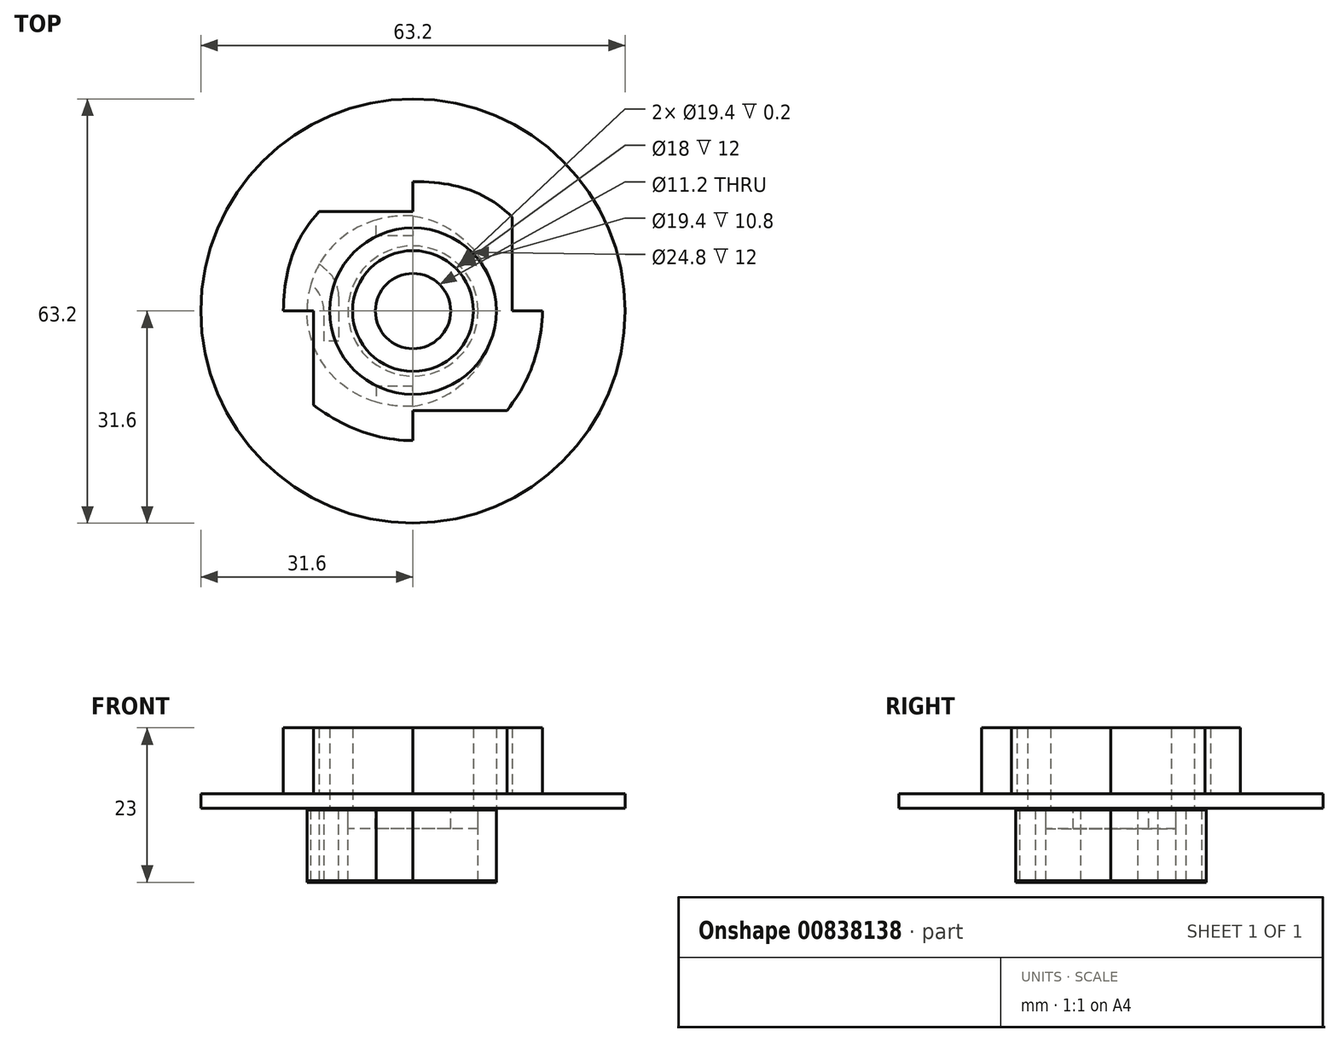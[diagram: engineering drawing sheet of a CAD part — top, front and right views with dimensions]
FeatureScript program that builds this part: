
annotation { "Feature Type Name" : "Feature", "Feature Type Description" : "" }
export const myFeature = defineFeature(function(context is Context, id is Id, definition is map)
    precondition{}
    {
        {
            var Q0;
            Q0=qCreatedBy(makeId("Top.planeOp"),FACE);
            var sketch = newSketch(context, id + "F0", { "sketchPlane" : qUnion([Q0])});
            skCircle(sketch, "E0", {"center": v(0, 0) * mm, "radius": 31.6 * mm});
            skCircle(sketch, "E1", {"center": v(0, 0) * mm, "radius": 5.5 * mm});
            skCircle(sketch, "E2", {"center": v(0, 0) * mm, "radius": 12.4 * mm});
            skCircle(sketch, "E3", {"center": v(0, 0) * mm, "radius": 14.8 * mm, "construction": true});
            skLineSegment(sketch, "E4", {"start": v(0, 14.8) * mm, "end": v(0, 19.3) * mm});
            skLineSegment(sketch, "E5", {"start": v(14.8, 14) * mm, "end": v(14.8, 0) * mm});
            skFitSpline(sketch, "E6", {"points": [v(0, 19.3) * mm, v(14.8, 14) * mm], "startDerivative": vector(19.32, -0.13) * mm, "endDerivative": vector(12.28, -11.69) * mm});
            skLineSegment(sketch, "E7.1.0", {"start": v(-14.8, 0) * mm, "end": v(-19.3, 0) * mm});
            skLineSegment(sketch, "E7.1.1", {"start": v(-14, 14.8) * mm, "end": v(0, 14.8) * mm});
            skLineSegment(sketch, "E7.2.0", {"start": v(0, -14.8) * mm, "end": v(0, -19.3) * mm});
            skLineSegment(sketch, "E7.2.1", {"start": v(-14.8, -14) * mm, "end": v(-14.8, 0) * mm});
            skLineSegment(sketch, "E8.1.3.0", {"start": v(14.8, 0) * mm, "end": v(19.3, 0) * mm});
            skLineSegment(sketch, "E8.3.3.0", {"start": v(14, -14.8) * mm, "end": v(0, -14.8) * mm});
            skFitSpline(sketch, "E9", {"points": [v(-14, 14.8) * mm, v(-19.3, 0) * mm], "startDerivative": vector(-12.02, -13.36) * mm, "endDerivative": vector(-0.47, -17.93) * mm});
            skFitSpline(sketch, "E10", {"points": [v(-14.8, -14) * mm, v(0, -19.3) * mm], "startDerivative": vector(12.93, -9.83) * mm, "endDerivative": vector(16.52, -0.04) * mm});
            skFitSpline(sketch, "E11", {"points": [v(14, -14.8) * mm, v(19.3, 0) * mm], "startDerivative": vector(10.45, 13.03) * mm, "endDerivative": vector(0.46, 16.43) * mm});
            skCircle(sketch, "E12", {"center": v(0, 0) * mm, "radius": 9 * mm});
            skSolve(sketch);
        }
        {
            var Q0;
            Q0=makeQuery(id+"F0.imprint","IMPRINT",FACE,{"disambiguationData":[TD([[makeQuery(id+"F0.imprint","IMPRINT",EDGE,{"derivedFrom":sQuery(id+"F0.wireOp",EDGE,"E2")}),-1.0]])]});
            extrude(context, id + "F1", {"entities" : qUnion([Q0]), "depth" : 12 * mm, "offsetDistance" : 25 * mm});
        }
        {
            var Q0;
            Q0=makeQuery(id+"F0.imprint","IMPRINT",FACE,{"disambiguationData":[TD([[makeQuery(id+"F0.imprint","IMPRINT",EDGE,{"derivedFrom":sQuery(id+"F0.wireOp",EDGE,"E0")}),1.0]])]});
            extrude(context, id + "F2", {"entities" : qUnion([Q0]), "operationType" : NewBodyOperationType.ADD, "depth" : (12 - 9.8) * mm, "offsetDistance" : 25 * mm});
        }
        {
            var Q0;
            Q0=makeQuery(id+"F0.imprint","IMPRINT",FACE,{"disambiguationData":[TD([[makeQuery(id+"F0.imprint","IMPRINT",EDGE,{"derivedFrom":sQuery(id+"F0.wireOp",EDGE,"E2")}),1.0]])]});
            extrude(context, id + "F3", {"entities" : qUnion([Q0]), "depth" : 12 * mm, "offsetDistance" : 25 * mm});
        }
        {
            var Q0;
            Q0=qCreatedBy(makeId("Top.planeOp"),FACE);
            var sketch = newSketch(context, id + "F4", { "sketchPlane" : qUnion([Q0])});
            skCircle(sketch, "E13", {"center": v(0, 0) * mm, "radius": 31.55 * mm});
            skCircle(sketch, "E14", {"center": v(0, 0) * mm, "radius": 9.7 * mm});
            skCircle(sketch, "E15", {"center": v(0, 0) * mm, "radius": 5.6 * mm});
            skLineSegment(sketch, "E16.MirrorCS", {"start": v(0, 0) * mm, "end": v(0, -14.2) * mm, "construction": true});
            skFitSpline(sketch, "E17", {"points": [v(0, 14.2) * mm, v(-15.8, 0) * mm], "startDerivative": vector(-27.93, 0.98) * mm, "endDerivative": vector(-0.29, -24.4) * mm});
            skFitSpline(sketch, "E18.MirrorCS", {"points": [v(0, -14.2) * mm, v(-15.8, 0) * mm], "startDerivative": vector(-27.93, -0.98) * mm, "endDerivative": vector(-0.29, 24.4) * mm});
            skLineSegment(sketch, "E19", {"start": v(-11.06, 0) * mm, "end": v(-11.06, -4.5) * mm});
            skLineSegment(sketch, "E20", {"start": v(-11.06, -4.5) * mm, "end": v(-13.26, -4.5) * mm});
            skLineSegment(sketch, "E21", {"start": v(-13.26, -4.5) * mm, "end": v(-13.26, 0) * mm});
            skLineSegment(sketch, "E22", {"start": v(-13.26, 0) * mm, "end": v(-13.26, 3) * mm});
            skLineSegment(sketch, "E23.MirrorCS", {"start": v(-11.06, 0) * mm, "end": v(-11.06, 4.5) * mm});
            skLineSegment(sketch, "E24", {"start": v(-13.95, 7) * mm, "end": v(-11.06, 4.5) * mm});
            skLineSegment(sketch, "E25", {"start": v(-15.21, 4) * mm, "end": v(-13.26, 3) * mm});
            skFitSpline(sketch, "E26", {"points": [v(0, 14.2) * mm, v(12.4, 0) * mm], "startDerivative": vector(22.88, -3.47) * mm, "endDerivative": vector(-0.26, -19.18) * mm});
            skFitSpline(sketch, "E27.MirrorCS", {"points": [v(0, -14.2) * mm, v(12.4, 0) * mm], "startDerivative": vector(22.88, 3.47) * mm, "endDerivative": vector(-0.26, 19.18) * mm});
            skLineSegment(sketch, "E28", {"start": v(0, 14.2) * mm, "end": v(0, 11.2) * mm});
            skLineSegment(sketch, "E29", {"start": v(0, 11.2) * mm, "end": v(-5.5, 11.2) * mm});
            skLineSegment(sketch, "E30", {"start": v(-5.5, 11.2) * mm, "end": v(-5.5, 13.55) * mm});
            skLineSegment(sketch, "E31.MirrorCS", {"start": v(-5.5, -11.2) * mm, "end": v(-5.5, -13.55) * mm});
            skLineSegment(sketch, "E32.MirrorCS", {"start": v(0, -11.2) * mm, "end": v(-5.5, -11.2) * mm});
            skLineSegment(sketch, "E33.MirrorCS", {"start": v(0, -14.2) * mm, "end": v(0, -11.2) * mm});
            skPoint(sketch, "E34", {"position": v(-1.7, 0) * mm});
            skCircle(sketch, "E35", {"center": v(-1.7, 0) * mm, "radius": 14.1 * mm, "construction": true});
            skSolve(sketch);
        }
        {
            var Q0;
            Q0=makeQuery(id+"F4.imprint","IMPRINT",FACE,{"disambiguationData":[TD([[makeQuery(id+"F4.imprint","IMPRINT",EDGE,{"derivedFrom":sQuery(id+"F4.wireOp",EDGE,"E19")}),-1.0]])]});
            extrude(context, id + "F5", {"entities" : qUnion([Q0]), "oppositeDirection" : true, "depth" : 25 * mm, "offsetDistance" : 25 * mm});
        }
        {
            var Q0;
            Q0=makeQuery(id+"F5.opExtrude","SWEPT_EDGE",EDGE,{"disambiguationData":[OSD([sQuery(id+"F4.wireOp",EDGE,"E23.MirrorCS"),sQuery(id+"F4.wireOp",EDGE,"E24")])]});
            var Q1;
            Q1=makeQuery(id+"F5.opExtrude","SWEPT_EDGE",EDGE,{"disambiguationData":[OSD([sQuery(id+"F4.wireOp",EDGE,"E22"),sQuery(id+"F4.wireOp",EDGE,"E25")])]});
            fillet(context, id + "F6", {"entities" : qUnion([Q0, Q1]), "radius" : 5 * mm, "tangentPropagation" : true, "allowEdgeOverflow" : false});
        }
        {
            var Q0;
            {var subQ2=sQuery(id+"F4.wireOp",EDGE,"E31.MirrorCS");Q0=makeQuery(id+"F4.imprint","IMPRINT",FACE,{"disambiguationData":[TD([[makeQuery(id+"F4.imprint","IMPRINT",EDGE,{"derivedFrom":subQ2}),1.0]])]});}
            var Q1;
            {var subQ0=sQuery(id+"F4.wireOp",EDGE,"E28");Q1=makeQuery(id+"F4.imprint","IMPRINT",FACE,{"disambiguationData":[TD([[makeQuery(id+"F4.imprint","IMPRINT",EDGE,{"derivedFrom":subQ0}),-1.0]])]});}
            extrude(context, id + "F7", {"entities" : qUnion([Q0, Q1]), "oppositeDirection" : true, "depth" : 25 * mm, "offsetDistance" : 25 * mm});
        }
        {
            var Q0;
            Q0=makeQuery(id+"F4.imprint","IMPRINT",FACE,{"disambiguationData":[TD([[makeQuery(id+"F4.imprint","IMPRINT",EDGE,{"derivedFrom":sQuery(id+"F4.wireOp",EDGE,"E14")}),1.0]])]});
            extrude(context, id + "F8", {"entities" : qUnion([Q0]), "oppositeDirection" : true, "depth" : 3 * mm, "offsetDistance" : 25 * mm});
        }
        {
            var Q0;
            Q0=makeQuery(id+"F4.imprint","IMPRINT",FACE,{"disambiguationData":[TD([[makeQuery(id+"F4.imprint","IMPRINT",EDGE,{"derivedFrom":sQuery(id+"F4.wireOp",EDGE,"E14")}),-1.0]])]});
            var Q1;
            Q1=makeQuery(id+"F4.imprint","IMPRINT",FACE,{"disambiguationData":[TD([[makeQuery(id+"F4.imprint","IMPRINT",EDGE,{"derivedFrom":sQuery(id+"F4.wireOp",EDGE,"E19")}),-1.0]])]});
            extrude(context, id + "F9", {"entities" : qUnion([Q0, Q1]), "oppositeDirection" : true, "depth" : (7.8 + 3) * mm, "offsetDistance" : 25 * mm});
        }
        {
            var Q0;
            Q0=makeQuery(id+"F5.opExtrude","SWEPT_BODY",BODY,{"disambiguationData":[OSD([sQuery(id+"F4.wireOp",EDGE,"E17"),sQuery(id+"F4.wireOp",EDGE,"E19"),sQuery(id+"F4.wireOp",EDGE,"E20"),sQuery(id+"F4.wireOp",EDGE,"E21"),sQuery(id+"F4.wireOp",EDGE,"E22"),sQuery(id+"F4.wireOp",EDGE,"E23.MirrorCS"),sQuery(id+"F4.wireOp",EDGE,"E24"),sQuery(id+"F4.wireOp",EDGE,"E25")])]});
            var Q1;
            Q1=makeQuery(id+"F7.opExtrude","SWEPT_BODY",BODY,{"disambiguationData":[OSD([sQuery(id+"F4.wireOp",EDGE,"E18.MirrorCS"),sQuery(id+"F4.wireOp",EDGE,"E31.MirrorCS"),sQuery(id+"F4.wireOp",EDGE,"E32.MirrorCS"),sQuery(id+"F4.wireOp",EDGE,"E33.MirrorCS")])]});
            var Q2;
            Q2=makeQuery(id+"F7.opExtrude","SWEPT_BODY",BODY,{"disambiguationData":[OSD([sQuery(id+"F4.wireOp",EDGE,"E17"),sQuery(id+"F4.wireOp",EDGE,"E28"),sQuery(id+"F4.wireOp",EDGE,"E29"),sQuery(id+"F4.wireOp",EDGE,"E30")])]});
            var Q3;
            Q3=makeQuery(id+"F9.opExtrude","SWEPT_BODY",BODY,{"disambiguationData":[OSD([sQuery(id+"F4.wireOp",EDGE,"E14"),sQuery(id+"F4.wireOp",EDGE,"E17"),sQuery(id+"F4.wireOp",EDGE,"E18.MirrorCS"),sQuery(id+"F4.wireOp",EDGE,"E26"),sQuery(id+"F4.wireOp",EDGE,"E27.MirrorCS"),sQuery(id+"F4.wireOp",EDGE,"E28"),sQuery(id+"F4.wireOp",EDGE,"E29"),sQuery(id+"F4.wireOp",EDGE,"E30"),sQuery(id+"F4.wireOp",EDGE,"E31.MirrorCS"),sQuery(id+"F4.wireOp",EDGE,"E32.MirrorCS"),sQuery(id+"F4.wireOp",EDGE,"E33.MirrorCS")])]});
            booleanBodies(context, id + "F10", {"operationType" : BooleanOperationType.SUBTRACTION, "tools" : qUnion([Q0, Q1, Q2]), "targets" : qUnion([Q3])});
        }
        {
            var Q0;
            Q0=makeQuery(id+"F4.imprint","IMPRINT",FACE,{"disambiguationData":[TD([[makeQuery(id+"F4.imprint","IMPRINT",EDGE,{"derivedFrom":sQuery(id+"F4.wireOp",EDGE,"E19")}),-1.0]])]});
            var Q1;
            {var subQ0=sQuery(id+"F4.wireOp",EDGE,"E28");Q1=makeQuery(id+"F4.imprint","IMPRINT",FACE,{"disambiguationData":[TD([[makeQuery(id+"F4.imprint","IMPRINT",EDGE,{"derivedFrom":subQ0}),-1.0]])]});}
            var Q2;
            {var subQ2=sQuery(id+"F4.wireOp",EDGE,"E31.MirrorCS");Q2=makeQuery(id+"F4.imprint","IMPRINT",FACE,{"disambiguationData":[TD([[makeQuery(id+"F4.imprint","IMPRINT",EDGE,{"derivedFrom":subQ2}),1.0]])]});}
            var Q3;
            Q3=makeQuery(id+"F9.opExtrude","CAP_FACE",FACE,{"disambiguationData":[OSD([sQuery(id+"F4.wireOp",EDGE,"E14"),sQuery(id+"F4.wireOp",EDGE,"E17"),sQuery(id+"F4.wireOp",EDGE,"E18.MirrorCS"),sQuery(id+"F4.wireOp",EDGE,"E26"),sQuery(id+"F4.wireOp",EDGE,"E27.MirrorCS"),sQuery(id+"F4.wireOp",EDGE,"E28"),sQuery(id+"F4.wireOp",EDGE,"E29"),sQuery(id+"F4.wireOp",EDGE,"E30"),sQuery(id+"F4.wireOp",EDGE,"E31.MirrorCS"),sQuery(id+"F4.wireOp",EDGE,"E32.MirrorCS"),sQuery(id+"F4.wireOp",EDGE,"E33.MirrorCS")])],"isStart":false});
            var Q4;
            Q4=makeQuery(id+"F4.imprint","IMPRINT",FACE,{"disambiguationData":[TD([[makeQuery(id+"F4.imprint","IMPRINT",EDGE,{"derivedFrom":sQuery(id+"F4.wireOp",EDGE,"E14")}),-1.0]])]});
            extrude(context, id + "F11", {"entities" : qUnion([Q0, Q1, Q2, Q3, Q4]), "oppositeDirection" : true, "depth" : 0.2 * mm, "offsetDistance" : 25 * mm});
        }
    });
